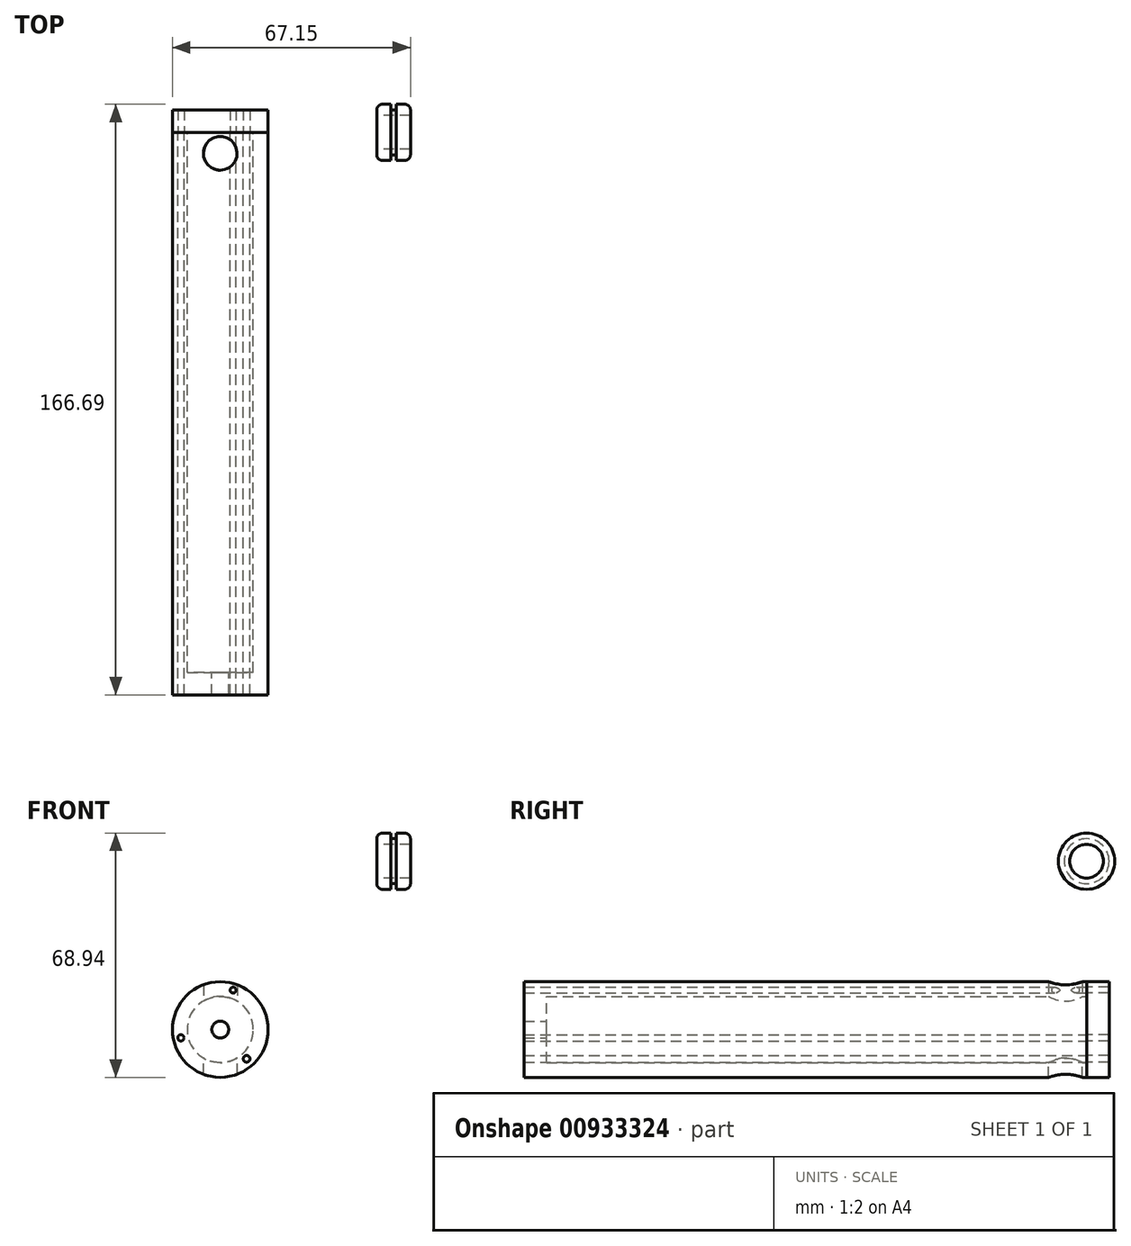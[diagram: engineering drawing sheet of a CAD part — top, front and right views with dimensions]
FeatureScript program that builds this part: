
annotation { "Feature Type Name" : "Feature", "Feature Type Description" : "" }
export const myFeature = defineFeature(function(context is Context, id is Id, definition is map)
    precondition{}
    {
        {
            var Q0;
            Q0=qCreatedBy(makeId("Front.planeOp"),FACE);
            var sketch = newSketch(context, id + "F0", { "sketchPlane" : qUnion([Q0])});
            skCircle(sketch, "E0", {"center": v(0, 0) * mm, "radius": 9.33 * mm});
            skCircle(sketch, "E1", {"center": v(0, 0) * mm, "radius": 13.5 * mm});
            skCircle(sketch, "E2.cCircle", {"center": v(0, 0) * mm, "radius": 6.36 * mm, "construction": true});
            skLineSegment(sketch, "E2.0", {"start": v(8.5, -9.46) * mm, "end": v(-12.44, -2.63) * mm, "construction": true});
            skLineSegment(sketch, "E2.1", {"start": v(-12.44, -2.63) * mm, "end": v(3.95, 12.09) * mm, "construction": true});
            skLineSegment(sketch, "E2.2", {"start": v(3.95, 12.09) * mm, "end": v(8.5, -9.46) * mm, "construction": true});
            skPoint(sketch, "E2.0.midPoint", {"position": v(-1.97, -6.04) * mm});
            skLineSegment(sketch, "E3", {"start": v(-12.44, -2.63) * mm, "end": v(0, 0) * mm, "construction": true});
            skLineSegment(sketch, "E4", {"start": v(3.95, 12.09) * mm, "end": v(0, 0) * mm, "construction": true});
            skLineSegment(sketch, "E5", {"start": v(8.5, -9.46) * mm, "end": v(0, 0) * mm, "construction": true});
            skCircle(sketch, "E6", {"center": v(7.42, -8.27) * mm, "radius": 0.93 * mm});
            skCircle(sketch, "E7", {"center": v(-11.11, -2.35) * mm, "radius": 0.88 * mm});
            skCircle(sketch, "E8", {"center": v(3.63, 11.11) * mm, "radius": 0.83 * mm});
            skSolve(sketch);
        }
        {
            var Q0;
            Q0=makeQuery(id+"F0.imprint","IMPRINT",FACE,{"disambiguationData":[TD([[makeQuery(id+"F0.imprint","IMPRINT",EDGE,{"derivedFrom":sQuery(id+"F0.wireOp",EDGE,"E0")}),-1.0]])]});
            extrude(context, id + "F1", {"entities" : qUnion([Q0]), "depth" : 152.4 * mm, "offsetDistance" : 25.4 * mm});
        }
        {
            var Q0;
            Q0=makeQuery(id+"F0.imprint","IMPRINT",FACE,{"disambiguationData":[TD([[makeQuery(id+"F0.imprint","IMPRINT",EDGE,{"derivedFrom":sQuery(id+"F0.wireOp",EDGE,"E0")}),-1.0]])]});
            var Q1;
            Q1=makeQuery(id+"F0.imprint","IMPRINT",FACE,{"disambiguationData":[TD([[makeQuery(id+"F0.imprint","IMPRINT",EDGE,{"derivedFrom":sQuery(id+"F0.wireOp",EDGE,"E0")}),1.0]])]});
            extrude(context, id + "F2", {"entities" : qUnion([Q0, Q1]), "oppositeDirection" : true, "depth" : 6.35 * mm, "offsetDistance" : 25.4 * mm});
        }
        {
            var Q0;
            Q0=makeQuery(id+"F1.opExtrude","CAP_FACE",FACE,{"disambiguationData":[OSD([sQuery(id+"F0.wireOp",EDGE,"E0"),sQuery(id+"F0.wireOp",EDGE,"E1")])],"isStart":false});
            var sketch = newSketch(context, id + "F3", { "sketchPlane" : qUnion([Q0])});
            skCircle(sketch, "E9", {"center": v(0, 0) * mm, "radius": 13.5 * mm});
            skCircle(sketch, "E10", {"center": v(0, 0) * mm, "radius": 2.38 * mm});
            skSolve(sketch);
        }
        {
            var Q0;
            Q0=makeQuery(id+"F3.imprint","IMPRINT",FACE,{"disambiguationData":[TD([[makeQuery(id+"F3.imprint","IMPRINT",EDGE,{"derivedFrom":sQuery(id+"F3.wireOp",EDGE,"E10")}),-1.0]])]});
            var Q1;
            Q1=makeQuery(id+"F3.imprint","IMPRINT",FACE,{"disambiguationData":[TD([[makeQuery(id+"F3.imprint","IMPRINT",EDGE,{"derivedFrom":sQuery(id+"F3.wireOp",EDGE,"E9")}),1.0]])]});
            extrude(context, id + "F4", {"entities" : qUnion([Q0, Q1]), "operationType" : NewBodyOperationType.ADD, "depth" : 6.35 * mm, "offsetDistance" : 25.4 * mm});
        }
        {
            var Q0;
            Q0=qCreatedBy(makeId("Front.planeOp"),FACE);
            var sketch = newSketch(context, id + "F5", { "sketchPlane" : qUnion([Q0])});
            skLineSegment(sketch, "E11", {"start": v(34.82, 47.5) * mm, "end": v(80.2, 47.5) * mm, "construction": true});
            skLineSegment(sketch, "E12.bottom", {"start": v(53.66, 39.57) * mm, "end": v(44.14, 39.57) * mm});
            skLineSegment(sketch, "E12.top", {"start": v(53.66, 55.45) * mm, "end": v(44.14, 55.45) * mm});
            skLineSegment(sketch, "E12.left", {"start": v(53.66, 39.57) * mm, "end": v(53.66, 55.45) * mm});
            skLineSegment(sketch, "E12.right", {"start": v(44.14, 39.57) * mm, "end": v(44.14, 55.45) * mm});
            skPoint(sketch, "E12.middle", {"position": v(48.9, 47.5) * mm});
            skLineSegment(sketch, "E13.bottom", {"start": v(48.1, 53.86) * mm, "end": v(49.7, 53.86) * mm});
            skLineSegment(sketch, "E13.top", {"start": v(48.1, 57.03) * mm, "end": v(49.7, 57.03) * mm});
            skLineSegment(sketch, "E13.left", {"start": v(48.1, 53.86) * mm, "end": v(48.1, 57.03) * mm});
            skLineSegment(sketch, "E13.right", {"start": v(49.7, 53.86) * mm, "end": v(49.7, 57.03) * mm});
            skPoint(sketch, "E13.middle", {"position": v(48.9, 55.45) * mm});
            skLineSegment(sketch, "E14.bottom", {"start": v(44.14, 42.75) * mm, "end": v(53.66, 42.75) * mm});
            skLineSegment(sketch, "E14.top", {"start": v(44.14, 52.27) * mm, "end": v(53.66, 52.27) * mm});
            skLineSegment(sketch, "E14.left", {"start": v(44.14, 42.75) * mm, "end": v(44.14, 52.27) * mm});
            skLineSegment(sketch, "E14.right", {"start": v(53.66, 42.75) * mm, "end": v(53.66, 52.27) * mm});
            skSolve(sketch);
        }
        {
            var Q0;
            {var subQ10=sQuery(id+"F5.wireOp",EDGE,"E13.bottom");Q0=makeQuery(id+"F5.imprint","IMPRINT",FACE,{"disambiguationData":[TD([[makeQuery(id+"F5.imprint","IMPRINT",EDGE,{"derivedFrom":subQ10}),-1.0]])]});}
            var Q1;
            Q1=sQuery(id+"F5.wireOp",EDGE,"E11");
            revolve(context, id + "F6", {"surfaceOperationType" : NewSurfaceOperationType.NEW, "entities" : qUnion([Q0]), "axis" : qUnion([Q1]), "revolveType" : RevolveType.FULL});
        }
        {
            var Q0;
            Q0=makeQuery(id+"F6.opRevolve","SWEPT_EDGE",EDGE,{"disambiguationData":[OSD([sQuery(id+"F5.wireOp",EDGE,"E12.top"),sQuery(id+"F5.wireOp",EDGE,"E12.right")])]});
            var Q1;
            Q1=makeQuery(id+"F6.opRevolve","SWEPT_EDGE",EDGE,{"disambiguationData":[OSD([sQuery(id+"F5.wireOp",EDGE,"E12.top"),sQuery(id+"F5.wireOp",EDGE,"E12.left")])]});
            fillet(context, id + "F7", {"entities" : qUnion([Q0, Q1]), "radius" : 1.65 * mm, "tangentPropagation" : true, "allowEdgeOverflow" : false});
        }
        {
            var Q0;
            Q0=qCreatedBy(makeId("Top.planeOp"),FACE);
            var sketch = newSketch(context, id + "F8", { "sketchPlane" : qUnion([Q0])});
            skCircle(sketch, "E15", {"center": v(0, -5.92) * mm, "radius": 4.76 * mm});
            skSolve(sketch);
        }
        {
            var Q0;
            Q0=sQuery(id+"F8.wireOp",VERTEX,"E15.center");
            var Q1;
            Q1=makeQuery(id+"F1.opExtrude","SWEPT_BODY",BODY,{"disambiguationData":[OSD([sQuery(id+"F0.wireOp",EDGE,"E0"),sQuery(id+"F0.wireOp",EDGE,"E1"),sQuery(id+"F0.wireOp",EDGE,"E6"),sQuery(id+"F0.wireOp",EDGE,"E7"),sQuery(id+"F0.wireOp",EDGE,"E8")])]});
            hole(context, id + "F9", {"style" : HoleStyle.SIMPLE, "endStyle" : HoleEndStyle.THROUGH, "oppositeDirection" : true, "holeDiameter" : 9.52 * mm, "majorDiameter" : 6.35 * mm, "isTappedThrough" : true, "tappedDepth" : 12.7 * mm, "tapClearance" : 3, "locations" : qUnion([Q0]), "scope" : qUnion([Q1])});
        }
        {
            var Q0;
            Q0=sQuery(id+"F8.wireOp",VERTEX,"E15.center");
            var Q1;
            Q1=makeQuery(id+"F1.opExtrude","SWEPT_BODY",BODY,{"disambiguationData":[OSD([sQuery(id+"F0.wireOp",EDGE,"E0"),sQuery(id+"F0.wireOp",EDGE,"E1"),sQuery(id+"F0.wireOp",EDGE,"E6"),sQuery(id+"F0.wireOp",EDGE,"E7"),sQuery(id+"F0.wireOp",EDGE,"E8")])]});
            hole(context, id + "F10", {"style" : HoleStyle.SIMPLE, "endStyle" : HoleEndStyle.THROUGH, "holeDiameter" : 9.52 * mm, "majorDiameter" : 6.35 * mm, "isTappedThrough" : true, "tappedDepth" : 12.7 * mm, "tapClearance" : 3, "locations" : qUnion([Q0]), "scope" : qUnion([Q1])});
        }
    });
